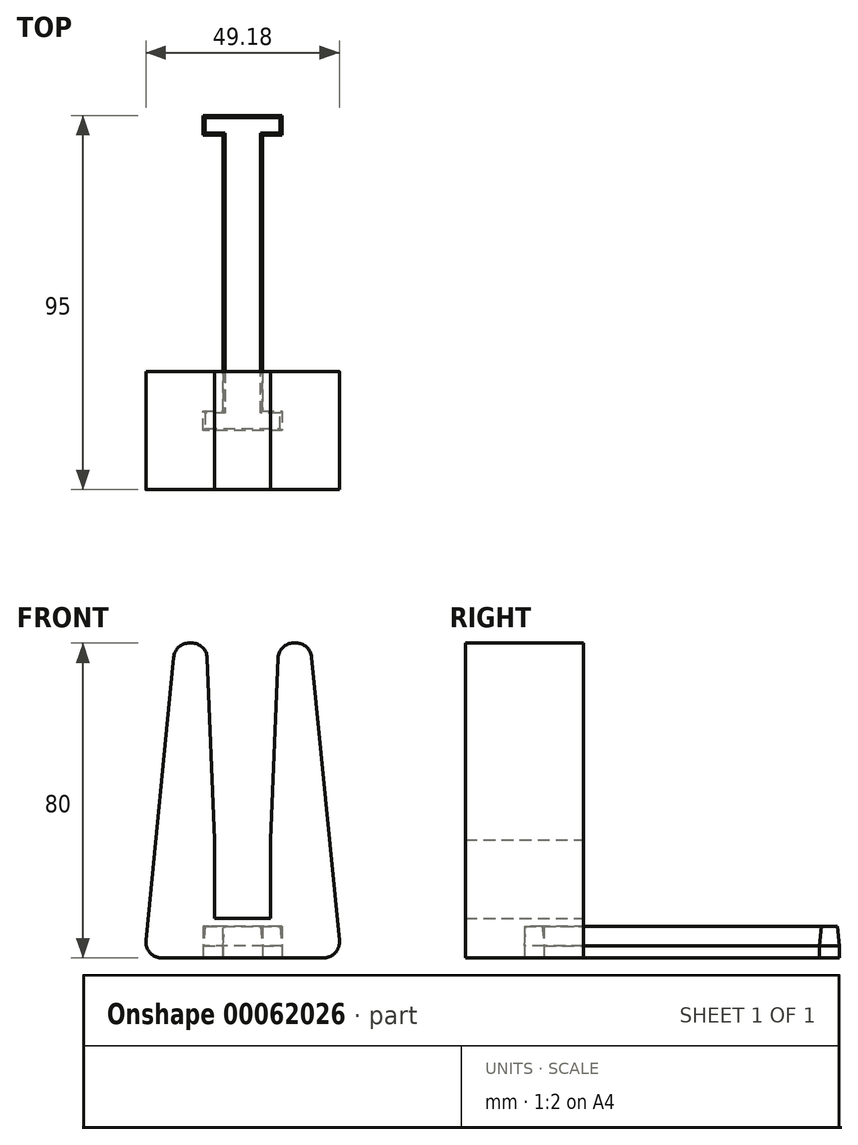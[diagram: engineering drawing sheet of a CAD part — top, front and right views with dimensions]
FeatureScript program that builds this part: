
annotation { "Feature Type Name" : "Feature", "Feature Type Description" : "" }
export const myFeature = defineFeature(function(context is Context, id is Id, definition is map)
    precondition{}
    {
        {
            var Q0;
            Q0=qCreatedBy(makeId("Front.planeOp"),FACE);
            var sketch = newSketch(context, id + "F0", { "sketchPlane" : qUnion([Q0])});
            skLineSegment(sketch, "E0", {"start": v(0, 0) * mm, "end": v(34.3, 0) * mm});
            skLineSegment(sketch, "E1", {"start": v(17.15, 0) * mm, "end": v(17.15, 10) * mm, "construction": true});
            skLineSegment(sketch, "E2", {"start": v(10, 10) * mm, "end": v(24.3, 10) * mm});
            skLineSegment(sketch, "E3", {"start": v(24.3, 10) * mm, "end": v(24.3, 80) * mm});
            skLineSegment(sketch, "E4", {"start": v(24.3, 80) * mm, "end": v(34.3, 80) * mm});
            skLineSegment(sketch, "E5", {"start": v(34.3, 80) * mm, "end": v(34.3, 0) * mm, "construction": true});
            skLineSegment(sketch, "E6.MirrorCS", {"start": v(10, 10) * mm, "end": v(10, 80) * mm});
            skLineSegment(sketch, "E7.MirrorCS", {"start": v(10, 80) * mm, "end": v(0, 80) * mm});
            skLineSegment(sketch, "E8.MirrorCS", {"start": v(0, 80) * mm, "end": v(0, 0) * mm, "construction": true});
            skLineSegment(sketch, "E9", {"start": v(34.3, 80) * mm, "end": v(42.15, 0) * mm});
            skLineSegment(sketch, "E10", {"start": v(42.15, 0) * mm, "end": v(34.3, 0) * mm});
            skLineSegment(sketch, "E11.MirrorCS", {"start": v(-7.85, 0) * mm, "end": v(0, 0) * mm});
            skLineSegment(sketch, "E12.MirrorCS", {"start": v(0, 80) * mm, "end": v(-7.85, 0) * mm});
            skSolve(sketch);
        }
        {
            var Q0;
            Q0=makeQuery(id+"F0.imprint","IMPRINT",FACE,{"disambiguationData":[TD([[makeQuery(id+"F0.imprint","IMPRINT",EDGE,{"derivedFrom":sQuery(id+"F0.wireOp",EDGE,"E0")}),1.0]])]});
            extrude(context, id + "F1", {"entities" : qUnion([Q0]), "depth" : 30 * mm});
        }
        {
            var Q0;
            Q0=makeQuery(id+"F1.opExtrude","SWEPT_FACE",FACE,{"disambiguationData":[OSD([sQuery(id+"F0.wireOp",EDGE,"E0"),sQuery(id+"F0.wireOp",EDGE,"E10"),sQuery(id+"F0.wireOp",EDGE,"E11.MirrorCS")])]});
            var sketch = newSketch(context, id + "F2", { "sketchPlane" : qUnion([Q0])});
            skLineSegment(sketch, "E13.bottom", {"start": v(42.15, 30) * mm, "end": v(-7.85, 30) * mm, "construction": true});
            skLineSegment(sketch, "E13.top", {"start": v(42.15, 0) * mm, "end": v(-7.85, 0) * mm, "construction": true});
            skLineSegment(sketch, "E13.left", {"start": v(42.15, 30) * mm, "end": v(42.15, 0) * mm, "construction": true});
            skLineSegment(sketch, "E13.right", {"start": v(-7.85, 30) * mm, "end": v(-7.85, 0) * mm, "construction": true});
            skPoint(sketch, "E14", {"position": v(17.15, 0) * mm});
            skLineSegment(sketch, "E15.rect.left", {"start": v(12.15, 0) * mm, "end": v(12.15, 10) * mm});
            skLineSegment(sketch, "E16.top", {"start": v(27.15, 15) * mm, "end": v(7.15, 15) * mm});
            skLineSegment(sketch, "E16.right", {"start": v(7.15, 10) * mm, "end": v(7.15, 15) * mm});
            skLineSegment(sketch, "E17", {"start": v(12.15, 10) * mm, "end": v(7.15, 10) * mm});
            skLineSegment(sketch, "E18", {"start": v(27.15, 15) * mm, "end": v(27.15, 10) * mm});
            skLineSegment(sketch, "E19", {"start": v(27.15, 10) * mm, "end": v(22.15, 10) * mm});
            skLineSegment(sketch, "E20", {"start": v(22.15, 10) * mm, "end": v(22.15, 0) * mm});
            skPoint(sketch, "E21", {"position": v(17.15, 15) * mm});
            skLineSegment(sketch, "E22", {"start": v(22.15, 0) * mm, "end": v(22.15, -50) * mm});
            skLineSegment(sketch, "E23", {"start": v(22.15, -50) * mm, "end": v(12.15, -50) * mm, "construction": true});
            skLineSegment(sketch, "E24", {"start": v(12.15, -50) * mm, "end": v(12.15, 0) * mm});
            skPoint(sketch, "E25", {"position": v(22.15, -25) * mm});
            skLineSegment(sketch, "E26", {"start": v(22.15, -25) * mm, "end": v(12.15, -25) * mm, "construction": true});
            skLineSegment(sketch, "E27.MirrorCS", {"start": v(12.15, -50) * mm, "end": v(12.15, -60) * mm});
            skLineSegment(sketch, "E28.MirrorCS", {"start": v(12.15, -60) * mm, "end": v(7.15, -60) * mm});
            skLineSegment(sketch, "E29.MirrorCS", {"start": v(7.15, -60) * mm, "end": v(7.15, -65) * mm});
            skLineSegment(sketch, "E30.MirrorCS", {"start": v(27.15, -65) * mm, "end": v(7.15, -65) * mm});
            skLineSegment(sketch, "E31.MirrorCS", {"start": v(27.15, -65) * mm, "end": v(27.15, -60) * mm});
            skLineSegment(sketch, "E32.MirrorCS", {"start": v(27.15, -60) * mm, "end": v(22.15, -60) * mm});
            skLineSegment(sketch, "E33.MirrorCS", {"start": v(22.15, -60) * mm, "end": v(22.15, -50) * mm});
            skSolve(sketch);
        }
        {
            var Q0;
            Q0 = qSketchRegion(id + "F2", true);
            extrude(context, id + "F3", {"entities" : qUnion([Q0]), "oppositeDirection" : true, "depth" : 8 * mm});
        }
        {
            var Q0;
            Q0=makeQuery(id+"F3.opExtrude","SWEPT_BODY",BODY,{"disambiguationData":[OSD([sQuery(id+"F2.wireOp",EDGE,"E15.rect.left"),sQuery(id+"F2.wireOp",EDGE,"E16.top"),sQuery(id+"F2.wireOp",EDGE,"E16.right"),sQuery(id+"F2.wireOp",EDGE,"E17"),sQuery(id+"F2.wireOp",EDGE,"E18"),sQuery(id+"F2.wireOp",EDGE,"E19"),sQuery(id+"F2.wireOp",EDGE,"E20"),sQuery(id+"F2.wireOp",EDGE,"E22"),sQuery(id+"F2.wireOp",EDGE,"E24"),sQuery(id+"F2.wireOp",EDGE,"E27.MirrorCS"),sQuery(id+"F2.wireOp",EDGE,"E28.MirrorCS"),sQuery(id+"F2.wireOp",EDGE,"E29.MirrorCS"),sQuery(id+"F2.wireOp",EDGE,"E30.MirrorCS"),sQuery(id+"F2.wireOp",EDGE,"E31.MirrorCS"),sQuery(id+"F2.wireOp",EDGE,"E32.MirrorCS"),sQuery(id+"F2.wireOp",EDGE,"E33.MirrorCS")])]});
            var Q1;
            Q1=makeQuery(id+"F1.opExtrude","SWEPT_BODY",BODY,{"disambiguationData":[OSD([sQuery(id+"F0.wireOp",EDGE,"E0"),sQuery(id+"F0.wireOp",EDGE,"E2"),sQuery(id+"F0.wireOp",EDGE,"E3"),sQuery(id+"F0.wireOp",EDGE,"E4"),sQuery(id+"F0.wireOp",EDGE,"E6.MirrorCS"),sQuery(id+"F0.wireOp",EDGE,"E7.MirrorCS"),sQuery(id+"F0.wireOp",EDGE,"E9"),sQuery(id+"F0.wireOp",EDGE,"E10"),sQuery(id+"F0.wireOp",EDGE,"E11.MirrorCS"),sQuery(id+"F0.wireOp",EDGE,"E12.MirrorCS")])]});
            booleanBodies(context, id + "F4", {"operationType" : BooleanOperationType.SUBTRACTION, "tools" : qUnion([Q0]), "targets" : qUnion([Q1]), "keepTools" : true});
        }
        {
            var Q0;
            Q0=makeQuery(id+"F1.opExtrude","SWEPT_EDGE",EDGE,{"disambiguationData":[OSD([sQuery(id+"F0.wireOp",EDGE,"E11.MirrorCS"),sQuery(id+"F0.wireOp",EDGE,"E12.MirrorCS")])]});
            var Q1;
            Q1=makeQuery(id+"F1.opExtrude","SWEPT_EDGE",EDGE,{"disambiguationData":[OSD([sQuery(id+"F0.wireOp",EDGE,"E9"),sQuery(id+"F0.wireOp",EDGE,"E10")])]});
            var Q2;
            Q2=makeQuery(id+"F1.opExtrude","SWEPT_EDGE",EDGE,{"disambiguationData":[OSD([sQuery(id+"F0.wireOp",EDGE,"E4"),sQuery(id+"F0.wireOp",EDGE,"E9")])]});
            var Q3;
            Q3=makeQuery(id+"F1.opExtrude","SWEPT_EDGE",EDGE,{"disambiguationData":[OSD([sQuery(id+"F0.wireOp",EDGE,"E7.MirrorCS"),sQuery(id+"F0.wireOp",EDGE,"E12.MirrorCS")])]});
            fillet(context, id + "F5", {"entities" : qUnion([Q0, Q1, Q2, Q3]), "radius" : 4 * mm, "tangentPropagation" : true, "allowEdgeOverflow" : false});
        }
        {
            var Q0;
            Q0=makeQuery(id+"F1.opExtrude","SWEPT_EDGE",EDGE,{"disambiguationData":[OSD([sQuery(id+"F0.wireOp",EDGE,"E6.MirrorCS"),sQuery(id+"F0.wireOp",EDGE,"E7.MirrorCS")])]});
            chamfer(context, id + "F6", {"entities" : qUnion([Q0]), "chamferType" : ChamferType.TWO_OFFSETS, "width1" : 2 * mm, "oppositeDirection" : false, "width2" : 50 * mm, "tangentPropagation" : true});
        }
        {
            var Q0;
            Q0=makeQuery(id+"F1.opExtrude","SWEPT_EDGE",EDGE,{"disambiguationData":[OSD([sQuery(id+"F0.wireOp",EDGE,"E3"),sQuery(id+"F0.wireOp",EDGE,"E4")])]});
            chamfer(context, id + "F7", {"entities" : qUnion([Q0]), "chamferType" : ChamferType.TWO_OFFSETS, "width1" : 50 * mm, "oppositeDirection" : false, "width2" : 2 * mm, "tangentPropagation" : true});
        }
        {
            var Q0;
            {var subQ0=sQuery(id+"F0.wireOp",EDGE,"E7.MirrorCS");Q0=makeQuery(id+"F6.opChamfer","BLEND_EDGE",EDGE,{"blendedFrom":[makeQuery(id+"F1.opExtrude","SWEPT_EDGE",EDGE,{"disambiguationData":[OSD([sQuery(id+"F0.wireOp",EDGE,"E6.MirrorCS"),subQ0])]}),makeQuery(id+"F1.opExtrude","SWEPT_FACE",FACE,{"disambiguationData":[OSD([subQ0])]})],"blendedInto":[makeQuery(id+"F1.opExtrude","SWEPT_FACE",FACE,{"disambiguationData":[OSD([subQ0])]})]});}
            var Q1;
            {var subQ0=sQuery(id+"F0.wireOp",EDGE,"E4");Q1=makeQuery(id+"F7.opChamfer","BLEND_EDGE",EDGE,{"blendedFrom":[makeQuery(id+"F1.opExtrude","SWEPT_EDGE",EDGE,{"disambiguationData":[OSD([sQuery(id+"F0.wireOp",EDGE,"E3"),subQ0])]}),makeQuery(id+"F1.opExtrude","SWEPT_FACE",FACE,{"disambiguationData":[OSD([subQ0])]})],"blendedInto":[makeQuery(id+"F1.opExtrude","SWEPT_FACE",FACE,{"disambiguationData":[OSD([subQ0])]})]});}
            fillet(context, id + "F8", {"entities" : qUnion([Q0, Q1]), "radius" : 4 * mm, "tangentPropagation" : true, "allowEdgeOverflow" : false});
        }
        {
            var Q0;
            Q0=makeQuery(id+"F3.opExtrude","CAP_EDGE",EDGE,{"disambiguationData":[OSD([sQuery(id+"F2.wireOp",EDGE,"E20"),sQuery(id+"F2.wireOp",EDGE,"E22"),sQuery(id+"F2.wireOp",EDGE,"E33.MirrorCS")])],"isStart":false});
            var Q1;
            Q1=makeQuery(id+"F3.opExtrude","CAP_EDGE",EDGE,{"disambiguationData":[OSD([sQuery(id+"F2.wireOp",EDGE,"E32.MirrorCS")])],"isStart":false});
            var Q2;
            Q2=makeQuery(id+"F3.opExtrude","CAP_EDGE",EDGE,{"disambiguationData":[OSD([sQuery(id+"F2.wireOp",EDGE,"E31.MirrorCS")])],"isStart":false});
            var Q3;
            Q3=makeQuery(id+"F3.opExtrude","CAP_EDGE",EDGE,{"disambiguationData":[OSD([sQuery(id+"F2.wireOp",EDGE,"E19")])],"isStart":false});
            var Q4;
            Q4=makeQuery(id+"F3.opExtrude","CAP_EDGE",EDGE,{"disambiguationData":[OSD([sQuery(id+"F2.wireOp",EDGE,"E18")])],"isStart":false});
            var Q5;
            Q5=makeQuery(id+"F3.opExtrude","CAP_EDGE",EDGE,{"disambiguationData":[OSD([sQuery(id+"F2.wireOp",EDGE,"E30.MirrorCS")])],"isStart":false});
            var Q6;
            Q6=makeQuery(id+"F3.opExtrude","CAP_EDGE",EDGE,{"disambiguationData":[OSD([sQuery(id+"F2.wireOp",EDGE,"E29.MirrorCS")])],"isStart":false});
            var Q7;
            Q7=makeQuery(id+"F3.opExtrude","CAP_EDGE",EDGE,{"disambiguationData":[OSD([sQuery(id+"F2.wireOp",EDGE,"E15.rect.left"),sQuery(id+"F2.wireOp",EDGE,"E24"),sQuery(id+"F2.wireOp",EDGE,"E27.MirrorCS")])],"isStart":false});
            var Q8;
            Q8=makeQuery(id+"F3.opExtrude","CAP_EDGE",EDGE,{"disambiguationData":[OSD([sQuery(id+"F2.wireOp",EDGE,"E17")])],"isStart":false});
            var Q9;
            Q9=makeQuery(id+"F3.opExtrude","CAP_EDGE",EDGE,{"disambiguationData":[OSD([sQuery(id+"F2.wireOp",EDGE,"E16.right")])],"isStart":false});
            var Q10;
            Q10=makeQuery(id+"F3.opExtrude","CAP_EDGE",EDGE,{"disambiguationData":[OSD([sQuery(id+"F2.wireOp",EDGE,"E28.MirrorCS")])],"isStart":false});
            var Q11;
            Q11=makeQuery(id+"F3.opExtrude","CAP_EDGE",EDGE,{"disambiguationData":[OSD([sQuery(id+"F2.wireOp",EDGE,"E16.top")])],"isStart":false});
            chamfer(context, id + "F9", {"entities" : qUnion([Q0, Q1, Q2, Q3, Q4, Q5, Q6, Q7, Q8, Q9, Q10, Q11]), "chamferType" : ChamferType.TWO_OFFSETS, "width1" : 0.5 * mm, "oppositeDirection" : false, "width2" : 5 * mm, "tangentPropagation" : true});
        }
    });
